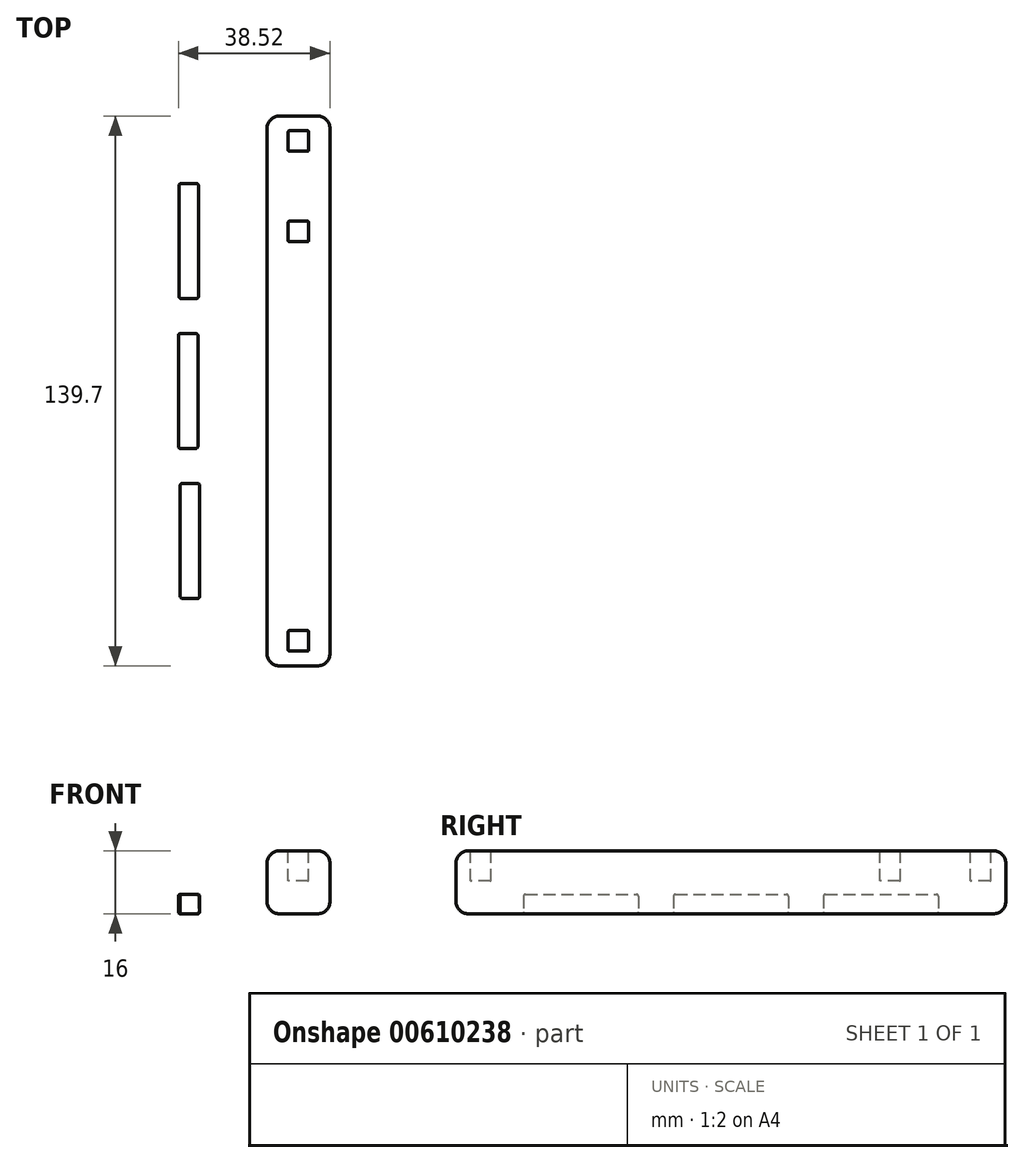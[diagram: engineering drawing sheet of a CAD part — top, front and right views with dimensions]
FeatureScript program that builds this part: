
annotation { "Feature Type Name" : "Feature", "Feature Type Description" : "" }
export const myFeature = defineFeature(function(context is Context, id is Id, definition is map)
    precondition{}
    {
        {
            var Q0;
            Q0=qCreatedBy(makeId("Front.planeOp"),FACE);
            var sketch = newSketch(context, id + "F0", { "sketchPlane" : qUnion([Q0])});
            skLineSegment(sketch, "E0.bottom", {"start": v(4.83, 0) * mm, "end": v(-4.83, 0) * mm});
            skLineSegment(sketch, "E0.top", {"start": v(4.83, 16) * mm, "end": v(-4.83, 16) * mm});
            skLineSegment(sketch, "E0.left", {"start": v(8, 3.18) * mm, "end": v(8, 12.83) * mm});
            skLineSegment(sketch, "E0.right", {"start": v(-8, 3.17) * mm, "end": v(-8, 12.83) * mm});
            skPoint(sketch, "E1.visualSharp", {"position": v(-8, 16) * mm});
            skArc(sketch, "E1.filletArc", {"start": v(-4.83, 16) * mm, "mid": v(-7.07, 15.07) * mm, "end": v(-8, 12.83) * mm});
            skPoint(sketch, "E2.visualSharp", {"position": v(8, 16) * mm});
            skArc(sketch, "E2.filletArc", {"start": v(8, 12.83) * mm, "mid": v(7.07, 15.07) * mm, "end": v(4.83, 16) * mm});
            skPoint(sketch, "E3.visualSharp", {"position": v(8, 0) * mm});
            skArc(sketch, "E3.filletArc", {"start": v(4.83, 0) * mm, "mid": v(7.07, 0.93) * mm, "end": v(8, 3.18) * mm});
            skPoint(sketch, "E4.visualSharp", {"position": v(-8, 0) * mm});
            skArc(sketch, "E4.filletArc", {"start": v(-8, 3.17) * mm, "mid": v(-7.07, 0.93) * mm, "end": v(-4.83, 0) * mm});
            skSolve(sketch);
        }
        {
            var Q0;
            Q0=makeQuery(id+"F0.imprint","IMPRINT",FACE,{"disambiguationData":[TD([[makeQuery(id+"F0.imprint","IMPRINT",EDGE,{"derivedFrom":sQuery(id+"F0.wireOp",EDGE,"E0.bottom")}),-1.0]])]});
            extrude(context, id + "F1", {"entities" : qUnion([Q0]), "endBound" : BoundingType.SYMMETRIC, "depth" : 139.7 * mm, "offsetDistance" : 25.4 * mm});
        }
        {
            var Q0;
            Q0=makeQuery(id+"F1.opExtrude","SWEPT_FACE",FACE,{"disambiguationData":[OSD([sQuery(id+"F0.wireOp",EDGE,"E0.top")])]});
            var sketch = newSketch(context, id + "F2", { "sketchPlane" : qUnion([Q0])});
            skLineSegment(sketch, "E5.bottom", {"start": v(2.35, 66.1) * mm, "end": v(-2.35, 66.1) * mm});
            skLineSegment(sketch, "E5.top", {"start": v(2.35, 60.9) * mm, "end": v(-2.35, 60.9) * mm});
            skLineSegment(sketch, "E5.left", {"start": v(2.6, 65.85) * mm, "end": v(2.6, 61.15) * mm});
            skLineSegment(sketch, "E5.right", {"start": v(-2.6, 65.85) * mm, "end": v(-2.6, 61.15) * mm});
            skPoint(sketch, "E5.middle", {"position": v(0, 63.5) * mm});
            skLineSegment(sketch, "E6.bottom", {"start": v(2.35, 43.12) * mm, "end": v(-2.35, 43.12) * mm});
            skLineSegment(sketch, "E6.top", {"start": v(2.35, 37.9) * mm, "end": v(-2.35, 37.9) * mm});
            skLineSegment(sketch, "E6.left", {"start": v(2.6, 42.86) * mm, "end": v(2.6, 38.16) * mm});
            skLineSegment(sketch, "E6.right", {"start": v(-2.6, 42.86) * mm, "end": v(-2.6, 38.16) * mm});
            skPoint(sketch, "E6.middle", {"position": v(0, 40.51) * mm});
            skLineSegment(sketch, "E7", {"start": v(0, -69.85) * mm, "end": v(0, -63.5) * mm});
            skLineSegment(sketch, "E8.bottom", {"start": v(2.35, -60.9) * mm, "end": v(-2.35, -60.9) * mm});
            skLineSegment(sketch, "E8.top", {"start": v(2.35, -66.1) * mm, "end": v(-2.35, -66.1) * mm});
            skLineSegment(sketch, "E8.left", {"start": v(2.6, -61.15) * mm, "end": v(2.6, -65.85) * mm});
            skLineSegment(sketch, "E8.right", {"start": v(-2.6, -61.15) * mm, "end": v(-2.6, -65.85) * mm});
            skPoint(sketch, "E8.middle", {"position": v(0, -63.5) * mm});
            skLineSegment(sketch, "E9", {"start": v(0, 69.85) * mm, "end": v(0, 63.5) * mm});
            skLineSegment(sketch, "E10", {"start": v(0, 60.9) * mm, "end": v(0, 43.12) * mm});
            skPoint(sketch, "E11.visualSharp", {"position": v(2.6, 66.1) * mm});
            skArc(sketch, "E11.filletArc", {"start": v(2.6, 65.85) * mm, "mid": v(2.53, 66.03) * mm, "end": v(2.35, 66.1) * mm});
            skPoint(sketch, "E12.visualSharp", {"position": v(-2.6, 66.1) * mm});
            skArc(sketch, "E12.filletArc", {"start": v(-2.35, 66.1) * mm, "mid": v(-2.53, 66.03) * mm, "end": v(-2.6, 65.85) * mm});
            skPoint(sketch, "E13.visualSharp", {"position": v(-2.6, 60.9) * mm});
            skArc(sketch, "E13.filletArc", {"start": v(-2.6, 61.15) * mm, "mid": v(-2.53, 60.97) * mm, "end": v(-2.35, 60.9) * mm});
            skPoint(sketch, "E14.visualSharp", {"position": v(2.6, 60.9) * mm});
            skArc(sketch, "E14.filletArc", {"start": v(2.35, 60.9) * mm, "mid": v(2.53, 60.97) * mm, "end": v(2.6, 61.15) * mm});
            skPoint(sketch, "E15.visualSharp", {"position": v(2.6, 43.12) * mm});
            skArc(sketch, "E15.filletArc", {"start": v(2.6, 42.86) * mm, "mid": v(2.53, 43.04) * mm, "end": v(2.35, 43.12) * mm});
            skPoint(sketch, "E16.visualSharp", {"position": v(2.6, 37.9) * mm});
            skArc(sketch, "E16.filletArc", {"start": v(2.35, 37.9) * mm, "mid": v(2.53, 37.98) * mm, "end": v(2.6, 38.16) * mm});
            skPoint(sketch, "E17.visualSharp", {"position": v(-2.6, 37.9) * mm});
            skArc(sketch, "E17.filletArc", {"start": v(-2.6, 38.16) * mm, "mid": v(-2.53, 37.98) * mm, "end": v(-2.35, 37.9) * mm});
            skPoint(sketch, "E18.visualSharp", {"position": v(-2.6, 43.12) * mm});
            skArc(sketch, "E18.filletArc", {"start": v(-2.35, 43.12) * mm, "mid": v(-2.53, 43.04) * mm, "end": v(-2.6, 42.86) * mm});
            skPoint(sketch, "E19.visualSharp", {"position": v(2.6, -60.9) * mm});
            skArc(sketch, "E19.filletArc", {"start": v(2.6, -61.15) * mm, "mid": v(2.53, -60.97) * mm, "end": v(2.35, -60.9) * mm});
            skPoint(sketch, "E20.visualSharp", {"position": v(2.6, -66.1) * mm});
            skArc(sketch, "E20.filletArc", {"start": v(2.35, -66.1) * mm, "mid": v(2.53, -66.03) * mm, "end": v(2.6, -65.85) * mm});
            skPoint(sketch, "E21.visualSharp", {"position": v(-2.6, -60.9) * mm});
            skArc(sketch, "E21.filletArc", {"start": v(-2.35, -60.9) * mm, "mid": v(-2.53, -60.97) * mm, "end": v(-2.6, -61.15) * mm});
            skPoint(sketch, "E22.visualSharp", {"position": v(-2.6, -66.1) * mm});
            skArc(sketch, "E22.filletArc", {"start": v(-2.6, -65.85) * mm, "mid": v(-2.53, -66.03) * mm, "end": v(-2.35, -66.1) * mm});
            skSolve(sketch);
        }
        {
            var Q0;
            Q0 = qSketchRegion(id + "F2", true);
            extrude(context, id + "F3", {"entities" : qUnion([Q0]), "operationType" : NewBodyOperationType.REMOVE, "oppositeDirection" : true, "depth" : 7.62 * mm, "offsetDistance" : 25.4 * mm});
        }
        {
            var Q0;
            Q0=qCreatedBy(makeId("Front.planeOp"),FACE);
            var sketch = newSketch(context, id + "F4", { "sketchPlane" : qUnion([Q0])});
            skLineSegment(sketch, "E23.bottom", {"start": v(-30.02, 4.95) * mm, "end": v(-26.08, 4.95) * mm});
            skLineSegment(sketch, "E23.top", {"start": v(-30.02, 0) * mm, "end": v(-26.08, 0) * mm});
            skLineSegment(sketch, "E23.left", {"start": v(-30.52, 4.45) * mm, "end": v(-30.52, 0.5) * mm});
            skLineSegment(sketch, "E23.right", {"start": v(-25.57, 4.45) * mm, "end": v(-25.57, 0.5) * mm});
            skPoint(sketch, "E24.visualSharp", {"position": v(-25.57, 4.95) * mm});
            skArc(sketch, "E24.filletArc", {"start": v(-25.57, 4.45) * mm, "mid": v(-25.72, 4.8) * mm, "end": v(-26.08, 4.95) * mm});
            skPoint(sketch, "E25.visualSharp", {"position": v(-25.57, 0) * mm});
            skArc(sketch, "E25.filletArc", {"start": v(-26.08, 0) * mm, "mid": v(-25.72, 0.15) * mm, "end": v(-25.57, 0.5) * mm});
            skPoint(sketch, "E26.visualSharp", {"position": v(-30.52, 4.95) * mm});
            skArc(sketch, "E26.filletArc", {"start": v(-30.02, 4.95) * mm, "mid": v(-30.38, 4.8) * mm, "end": v(-30.52, 4.45) * mm});
            skPoint(sketch, "E27.visualSharp", {"position": v(-30.52, 0) * mm});
            skArc(sketch, "E27.filletArc", {"start": v(-30.52, 0.5) * mm, "mid": v(-30.38, 0.15) * mm, "end": v(-30.02, 0) * mm});
            skLineSegment(sketch, "E28.bottom", {"start": v(-15.9, 4.95) * mm, "end": v(-11.96, 4.95) * mm});
            skLineSegment(sketch, "E28.top", {"start": v(-15.9, 0) * mm, "end": v(-11.96, 0) * mm});
            skLineSegment(sketch, "E28.left", {"start": v(-16.4, 4.45) * mm, "end": v(-16.4, 0.5) * mm});
            skLineSegment(sketch, "E28.right", {"start": v(-11.45, 4.45) * mm, "end": v(-11.45, 0.5) * mm});
            skPoint(sketch, "E29.visualSharp", {"position": v(-11.45, 4.95) * mm});
            skArc(sketch, "E29.filletArc", {"start": v(-11.45, 4.45) * mm, "mid": v(-11.6, 4.8) * mm, "end": v(-11.96, 4.95) * mm});
            skPoint(sketch, "E30.visualSharp", {"position": v(-11.45, 0) * mm});
            skArc(sketch, "E30.filletArc", {"start": v(-11.96, 0) * mm, "mid": v(-11.6, 0.15) * mm, "end": v(-11.45, 0.5) * mm});
            skPoint(sketch, "E31.visualSharp", {"position": v(-16.4, 4.95) * mm});
            skArc(sketch, "E31.filletArc", {"start": v(-15.9, 4.95) * mm, "mid": v(-16.25, 4.8) * mm, "end": v(-16.4, 4.45) * mm});
            skPoint(sketch, "E32.visualSharp", {"position": v(-16.4, 0) * mm});
            skArc(sketch, "E32.filletArc", {"start": v(-16.4, 0.5) * mm, "mid": v(-16.25, 0.15) * mm, "end": v(-15.9, 0) * mm});
            skLineSegment(sketch, "E33.bottom", {"start": v(-43.5, 4.95) * mm, "end": v(-39.57, 4.95) * mm});
            skLineSegment(sketch, "E33.top", {"start": v(-43.5, 0) * mm, "end": v(-39.57, 0) * mm});
            skLineSegment(sketch, "E33.left", {"start": v(-44.01, 4.45) * mm, "end": v(-44.01, 0.5) * mm});
            skLineSegment(sketch, "E33.right", {"start": v(-39.06, 4.45) * mm, "end": v(-39.06, 0.5) * mm});
            skPoint(sketch, "E34.visualSharp", {"position": v(-39.06, 4.95) * mm});
            skArc(sketch, "E34.filletArc", {"start": v(-39.06, 4.45) * mm, "mid": v(-39.2, 4.8) * mm, "end": v(-39.57, 4.95) * mm});
            skPoint(sketch, "E35.visualSharp", {"position": v(-39.06, 0) * mm});
            skArc(sketch, "E35.filletArc", {"start": v(-39.57, 0) * mm, "mid": v(-39.2, 0.15) * mm, "end": v(-39.06, 0.5) * mm});
            skPoint(sketch, "E36.visualSharp", {"position": v(-44.01, 4.95) * mm});
            skArc(sketch, "E36.filletArc", {"start": v(-43.5, 4.95) * mm, "mid": v(-43.86, 4.8) * mm, "end": v(-44.01, 4.45) * mm});
            skPoint(sketch, "E37.visualSharp", {"position": v(-44.01, 0) * mm});
            skArc(sketch, "E37.filletArc", {"start": v(-44.01, 0.5) * mm, "mid": v(-43.86, 0.15) * mm, "end": v(-43.5, 0) * mm});
            skSolve(sketch);
        }
        {
            var Q0;
            Q0 = qSketchRegion(id + "F4", true);
            extrude(context, id + "F5", {"entities" : qUnion([Q0]), "endBound" : BoundingType.SYMMETRIC, "depth" : 29.2 * mm, "offsetDistance" : 25.4 * mm});
        }
        {
            var Q0;
            Q0=makeQuery(id+"F5.opExtrude","CAP_FACE",FACE,{"disambiguationData":[OSD([sQuery(id+"F4.wireOp",EDGE,"E33.bottom"),sQuery(id+"F4.wireOp",EDGE,"E33.top"),sQuery(id+"F4.wireOp",EDGE,"E33.left"),sQuery(id+"F4.wireOp",EDGE,"E33.right"),sQuery(id+"F4.wireOp",EDGE,"E34.filletArc"),sQuery(id+"F4.wireOp",EDGE,"E35.filletArc"),sQuery(id+"F4.wireOp",EDGE,"E36.filletArc"),sQuery(id+"F4.wireOp",EDGE,"E37.filletArc")])],"isStart":false});
            var Q1;
            Q1=makeQuery(id+"F5.opExtrude","CAP_FACE",FACE,{"disambiguationData":[OSD([sQuery(id+"F4.wireOp",EDGE,"E23.bottom"),sQuery(id+"F4.wireOp",EDGE,"E23.top"),sQuery(id+"F4.wireOp",EDGE,"E23.left"),sQuery(id+"F4.wireOp",EDGE,"E23.right"),sQuery(id+"F4.wireOp",EDGE,"E24.filletArc"),sQuery(id+"F4.wireOp",EDGE,"E25.filletArc"),sQuery(id+"F4.wireOp",EDGE,"E26.filletArc"),sQuery(id+"F4.wireOp",EDGE,"E27.filletArc")])],"isStart":false});
            var Q2;
            Q2=makeQuery(id+"F5.opExtrude","CAP_FACE",FACE,{"disambiguationData":[OSD([sQuery(id+"F4.wireOp",EDGE,"E28.bottom"),sQuery(id+"F4.wireOp",EDGE,"E28.top"),sQuery(id+"F4.wireOp",EDGE,"E28.left"),sQuery(id+"F4.wireOp",EDGE,"E28.right"),sQuery(id+"F4.wireOp",EDGE,"E29.filletArc"),sQuery(id+"F4.wireOp",EDGE,"E30.filletArc"),sQuery(id+"F4.wireOp",EDGE,"E31.filletArc"),sQuery(id+"F4.wireOp",EDGE,"E32.filletArc")])],"isStart":false});
            var Q3;
            Q3=makeQuery(id+"F5.opExtrude","CAP_FACE",FACE,{"disambiguationData":[OSD([sQuery(id+"F4.wireOp",EDGE,"E28.bottom"),sQuery(id+"F4.wireOp",EDGE,"E28.top"),sQuery(id+"F4.wireOp",EDGE,"E28.left"),sQuery(id+"F4.wireOp",EDGE,"E28.right"),sQuery(id+"F4.wireOp",EDGE,"E29.filletArc"),sQuery(id+"F4.wireOp",EDGE,"E30.filletArc"),sQuery(id+"F4.wireOp",EDGE,"E31.filletArc"),sQuery(id+"F4.wireOp",EDGE,"E32.filletArc")])],"isStart":true});
            var Q4;
            Q4=makeQuery(id+"F5.opExtrude","CAP_FACE",FACE,{"disambiguationData":[OSD([sQuery(id+"F4.wireOp",EDGE,"E23.bottom"),sQuery(id+"F4.wireOp",EDGE,"E23.top"),sQuery(id+"F4.wireOp",EDGE,"E23.left"),sQuery(id+"F4.wireOp",EDGE,"E23.right"),sQuery(id+"F4.wireOp",EDGE,"E24.filletArc"),sQuery(id+"F4.wireOp",EDGE,"E25.filletArc"),sQuery(id+"F4.wireOp",EDGE,"E26.filletArc"),sQuery(id+"F4.wireOp",EDGE,"E27.filletArc")])],"isStart":true});
            var Q5;
            Q5=makeQuery(id+"F5.opExtrude","CAP_FACE",FACE,{"disambiguationData":[OSD([sQuery(id+"F4.wireOp",EDGE,"E33.bottom"),sQuery(id+"F4.wireOp",EDGE,"E33.top"),sQuery(id+"F4.wireOp",EDGE,"E33.left"),sQuery(id+"F4.wireOp",EDGE,"E33.right"),sQuery(id+"F4.wireOp",EDGE,"E34.filletArc"),sQuery(id+"F4.wireOp",EDGE,"E35.filletArc"),sQuery(id+"F4.wireOp",EDGE,"E36.filletArc"),sQuery(id+"F4.wireOp",EDGE,"E37.filletArc")])],"isStart":true});
            fillet(context, id + "F6", {"entities" : qUnion([Q0, Q1, Q2, Q3, Q4, Q5]), "radius" : 0.5 * mm, "tangentPropagation" : true, "allowEdgeOverflow" : false});
        }
        {
            var Q0;
            Q0=makeQuery(id+"F1.opExtrude","CAP_FACE",FACE,{"disambiguationData":[OSD([sQuery(id+"F0.wireOp",EDGE,"E0.bottom"),sQuery(id+"F0.wireOp",EDGE,"E0.top"),sQuery(id+"F0.wireOp",EDGE,"E0.left"),sQuery(id+"F0.wireOp",EDGE,"E0.right"),sQuery(id+"F0.wireOp",EDGE,"E1.filletArc"),sQuery(id+"F0.wireOp",EDGE,"E2.filletArc"),sQuery(id+"F0.wireOp",EDGE,"E3.filletArc"),sQuery(id+"F0.wireOp",EDGE,"E4.filletArc")])],"isStart":true});
            var Q1;
            Q1=makeQuery(id+"F1.opExtrude","CAP_FACE",FACE,{"disambiguationData":[OSD([sQuery(id+"F0.wireOp",EDGE,"E0.bottom"),sQuery(id+"F0.wireOp",EDGE,"E0.top"),sQuery(id+"F0.wireOp",EDGE,"E0.left"),sQuery(id+"F0.wireOp",EDGE,"E0.right"),sQuery(id+"F0.wireOp",EDGE,"E1.filletArc"),sQuery(id+"F0.wireOp",EDGE,"E2.filletArc"),sQuery(id+"F0.wireOp",EDGE,"E3.filletArc"),sQuery(id+"F0.wireOp",EDGE,"E4.filletArc")])],"isStart":false});
            fillet(context, id + "F7", {"entities" : qUnion([Q0, Q1]), "radius" : 3.17 * mm, "tangentPropagation" : true, "allowEdgeOverflow" : false});
        }
        {
            var Q0;
            Q0=makeQuery(id+"F5.opExtrude","SWEPT_BODY",BODY,{"disambiguationData":[OSD([sQuery(id+"F4.wireOp",EDGE,"E28.bottom"),sQuery(id+"F4.wireOp",EDGE,"E28.top"),sQuery(id+"F4.wireOp",EDGE,"E28.left"),sQuery(id+"F4.wireOp",EDGE,"E28.right"),sQuery(id+"F4.wireOp",EDGE,"E29.filletArc"),sQuery(id+"F4.wireOp",EDGE,"E30.filletArc"),sQuery(id+"F4.wireOp",EDGE,"E31.filletArc"),sQuery(id+"F4.wireOp",EDGE,"E32.filletArc")])]});
            transform(context, id + "F8", {"entities" : qUnion([Q0]), "transformType" : TransformType.TRANSLATION_3D, "dx" : -13.97 * mm, "dy" : 38.1 * mm, "dz" : 0 * mm, "makeCopy" : false});
        }
        {
            var Q0;
            Q0=makeQuery(id+"F5.opExtrude","SWEPT_BODY",BODY,{"disambiguationData":[OSD([sQuery(id+"F4.wireOp",EDGE,"E33.bottom"),sQuery(id+"F4.wireOp",EDGE,"E33.top"),sQuery(id+"F4.wireOp",EDGE,"E33.left"),sQuery(id+"F4.wireOp",EDGE,"E33.right"),sQuery(id+"F4.wireOp",EDGE,"E34.filletArc"),sQuery(id+"F4.wireOp",EDGE,"E35.filletArc"),sQuery(id+"F4.wireOp",EDGE,"E36.filletArc"),sQuery(id+"F4.wireOp",EDGE,"E37.filletArc")])]});
            transform(context, id + "F9", {"entities" : qUnion([Q0]), "transformType" : TransformType.TRANSLATION_3D, "dx" : 13.97 * mm, "dy" : -38.1 * mm, "dz" : 0 * mm, "makeCopy" : false});
        }
    });
